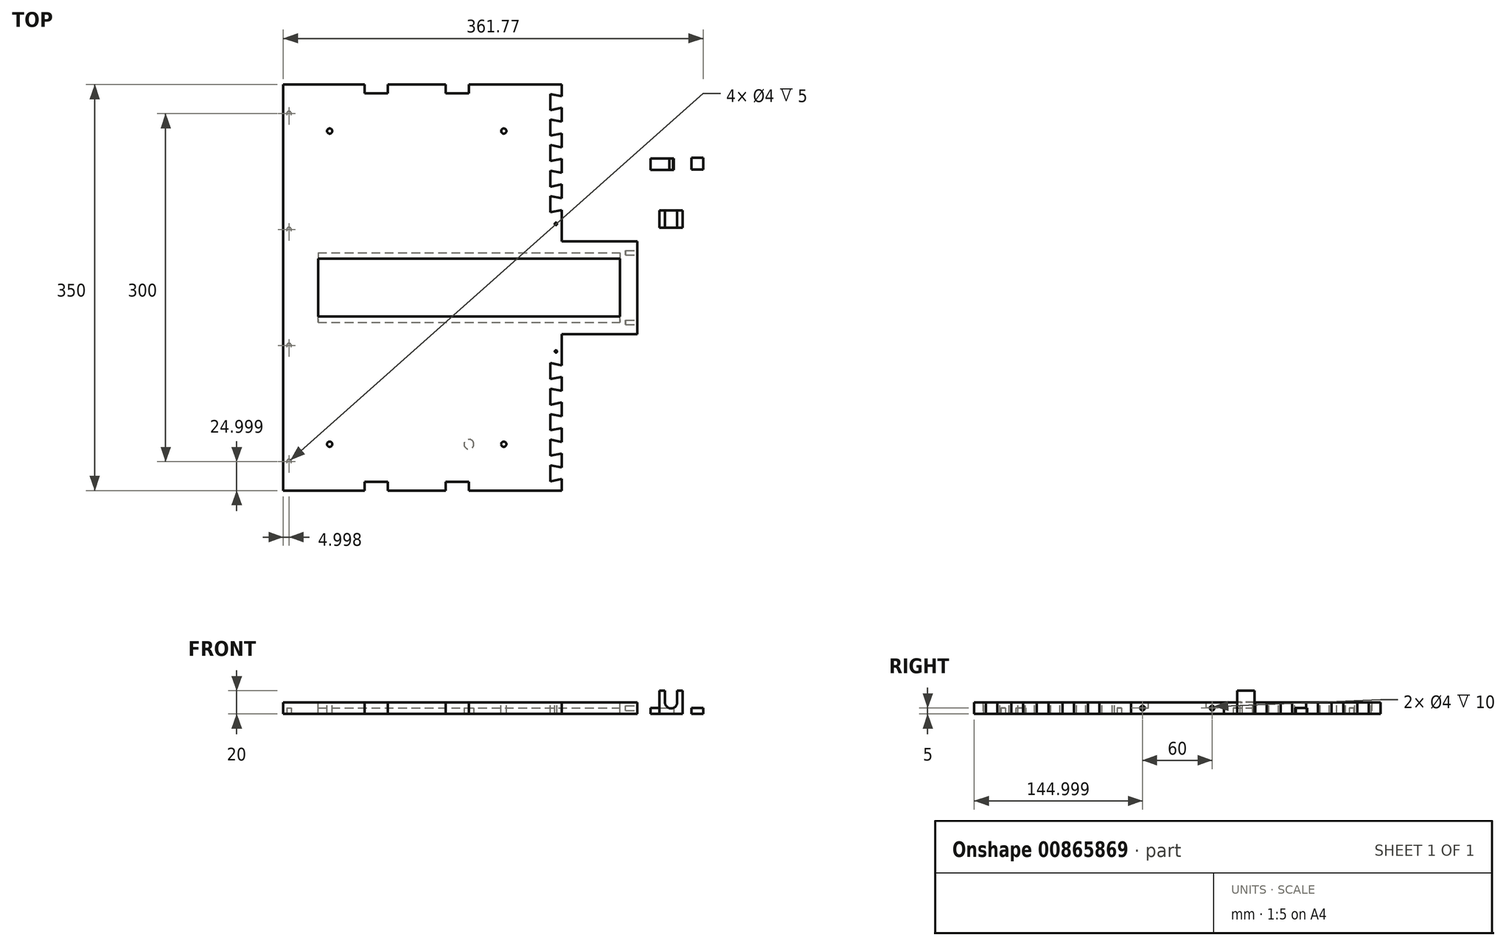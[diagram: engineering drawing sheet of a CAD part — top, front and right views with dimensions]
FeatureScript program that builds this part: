
annotation { "Feature Type Name" : "Feature", "Feature Type Description" : "" }
export const myFeature = defineFeature(function(context is Context, id is Id, definition is map)
    precondition{}
    {
        {
            var Q0;
            Q0=qCreatedBy(makeId("Top.planeOp"),FACE);
            var sketch = newSketch(context, id + "F0", { "sketchPlane" : qUnion([Q0])});
            skLineSegment(sketch, "E0.bottom", {"start": v(-223.21, 173.04) * mm, "end": v(-153.21, 173.04) * mm});
            skLineSegment(sketch, "E0.top", {"start": v(-223.21, -176.96) * mm, "end": v(-153.21, -176.96) * mm});
            skLineSegment(sketch, "E0.left", {"start": v(-223.21, 173.04) * mm, "end": v(-223.21, -176.96) * mm});
            skLineSegment(sketch, "E1.bottom", {"start": v(16.79, 38.04) * mm, "end": v(81.79, 38.04) * mm});
            skLineSegment(sketch, "E1.top", {"start": v(16.79, -41.96) * mm, "end": v(81.79, -41.96) * mm});
            skLineSegment(sketch, "E1.right", {"start": v(81.79, 38.04) * mm, "end": v(81.79, -41.96) * mm});
            skLineSegment(sketch, "E2", {"start": v(-153.21, -176.96) * mm, "end": v(-153.21, -169.46) * mm});
            skLineSegment(sketch, "E3", {"start": v(-153.21, -169.46) * mm, "end": v(-133.21, -169.46) * mm});
            skLineSegment(sketch, "E4", {"start": v(-133.21, -169.46) * mm, "end": v(-133.21, -176.96) * mm});
            skLineSegment(sketch, "E5", {"start": v(-83.21, -176.96) * mm, "end": v(-83.21, -169.46) * mm});
            skLineSegment(sketch, "E6", {"start": v(-83.21, -169.46) * mm, "end": v(-63.21, -169.46) * mm});
            skLineSegment(sketch, "E7", {"start": v(-63.21, -169.46) * mm, "end": v(-63.21, -176.96) * mm});
            skLineSegment(sketch, "E8", {"start": v(-153.21, 173.04) * mm, "end": v(-153.21, 165.54) * mm});
            skLineSegment(sketch, "E9", {"start": v(-153.21, 165.54) * mm, "end": v(-133.21, 165.54) * mm});
            skLineSegment(sketch, "E10", {"start": v(-133.21, 165.54) * mm, "end": v(-133.21, 173.04) * mm});
            skLineSegment(sketch, "E11", {"start": v(-83.21, 173.04) * mm, "end": v(-83.21, 165.54) * mm});
            skLineSegment(sketch, "E12", {"start": v(-83.21, 165.54) * mm, "end": v(-63.21, 165.54) * mm});
            skLineSegment(sketch, "E13", {"start": v(-63.21, 165.54) * mm, "end": v(-63.21, 173.04) * mm});
            skLineSegment(sketch, "E14.trimOffspring", {"start": v(-133.21, 173.04) * mm, "end": v(-83.21, 173.04) * mm});
            skLineSegment(sketch, "E15.trimOffspring", {"start": v(-63.21, 173.04) * mm, "end": v(16.79, 173.04) * mm});
            skLineSegment(sketch, "E16.trimOffspring", {"start": v(-133.21, -176.96) * mm, "end": v(-83.21, -176.96) * mm});
            skLineSegment(sketch, "E17.trimOffspring", {"start": v(-63.21, -176.96) * mm, "end": v(16.79, -176.96) * mm});
            skLineSegment(sketch, "E18", {"start": v(16.79, -41.96) * mm, "end": v(16.79, -176.96) * mm});
            skLineSegment(sketch, "E19", {"start": v(16.79, 173.04) * mm, "end": v(16.79, 38.04) * mm});
            skSolve(sketch);
        }
        {
            var Q0;
            Q0 = qSketchRegion(id + "F0", true);
            extrude(context, id + "F1", {"entities" : qUnion([Q0]), "depth" : 10 * mm, "offsetDistance" : 25 * mm});
        }
        {
            var Q0;
            Q0=makeQuery(id+"F1.opExtrude","CAP_FACE",FACE,{"disambiguationData":[OSD([sQuery(id+"F0.wireOp",EDGE,"E0.bottom"),sQuery(id+"F0.wireOp",EDGE,"E0.top"),sQuery(id+"F0.wireOp",EDGE,"E0.left"),sQuery(id+"F0.wireOp",EDGE,"E0.right"),sQuery(id+"F0.wireOp",EDGE,"E1.bottom"),sQuery(id+"F0.wireOp",EDGE,"E1.top"),sQuery(id+"F0.wireOp",EDGE,"E1.right"),sQuery(id+"F0.wireOp",EDGE,"E2"),sQuery(id+"F0.wireOp",EDGE,"E3"),sQuery(id+"F0.wireOp",EDGE,"E4"),sQuery(id+"F0.wireOp",EDGE,"E5"),sQuery(id+"F0.wireOp",EDGE,"E6"),sQuery(id+"F0.wireOp",EDGE,"E7"),sQuery(id+"F0.wireOp",EDGE,"E8"),sQuery(id+"F0.wireOp",EDGE,"E9"),sQuery(id+"F0.wireOp",EDGE,"E10"),sQuery(id+"F0.wireOp",EDGE,"E11"),sQuery(id+"F0.wireOp",EDGE,"E12"),sQuery(id+"F0.wireOp",EDGE,"E13"),sQuery(id+"F0.wireOp",EDGE,"E14.trimOffspring"),sQuery(id+"F0.wireOp",EDGE,"E15.trimOffspring"),sQuery(id+"F0.wireOp",EDGE,"E16.trimOffspring"),sQuery(id+"F0.wireOp",EDGE,"E17.trimOffspring"),sQuery(id+"F0.wireOp",EDGE,"d612cc93-a2dd-4ca0-8a1d-24db4bd78f01.trimOffspring"),sQuery(id+"F0.wireOp",EDGE,"VUu9vlwh-scEU-5erY-qjFF-pzVOPnd5OPAv"),sQuery(id+"F0.wireOp",EDGE,"Mesl0YVq-1EAC-d2jV-bsOK-wMALHSYDG3NM"),sQuery(id+"F0.wireOp",EDGE,"92T8g2C6-nla1-RGQU-U8xP-0400sJSxDG5c"),sQuery(id+"F0.wireOp",EDGE,"8OttDziy-c3AC-nBwE-2vRi-LbN1xkyNv4S0"),sQuery(id+"F0.wireOp",EDGE,"olr9cFaj-wmcz-6iY7-7Rzk-0wIROpixpfNE"),sQuery(id+"F0.wireOp",EDGE,"gA334X8u-PkTN-EDb3-7s9l-FT2O3QUcBCii"),sQuery(id+"F0.wireOp",EDGE,"2W5brfAA-w2qS-zJ9u-xPJi-NcULJrRPswGo"),sQuery(id+"F0.wireOp",EDGE,"luCa4cxE-H1tV-c6ab-pDNL-xg3xlzjdEsyn"),sQuery(id+"F0.wireOp",EDGE,"lG8ZVKkz-6INt-8FFC-6SXb-zNrBTEiRuwl3"),sQuery(id+"F0.wireOp",EDGE,"XRRxn0Ou-MKkb-N5V8-Fc5L-teCLoHKRe5wq"),sQuery(id+"F0.wireOp",EDGE,"wRixlGXv-lyk0-Hawx-yPcE-yobWA8MM16vS"),sQuery(id+"F0.wireOp",EDGE,"6DYoSN1p-wePG-CHtV-O8LX-gUoD5BVTUscE"),sQuery(id+"F0.wireOp",EDGE,"7xG2Ml0I-4bGv-ebdC-AR4S-G1sii3d71s1m"),sQuery(id+"F0.wireOp",EDGE,"Riv4Mbvf-Fbdf-Y5cd-fsFX-eB2JetC9W9YG"),sQuery(id+"F0.wireOp",EDGE,"No0oerPV-7ng4-ggHj-k2Vg-0BrW91tESk6H"),sQuery(id+"F0.wireOp",EDGE,"f2yUet7i-MCtZ-KdoX-q0Co-NCC2tnTZev2N"),sQuery(id+"F0.wireOp",EDGE,"cGX4Fyby-ReKv-VlGi-A0E8-5zCFY62Pwgkj"),sQuery(id+"F0.wireOp",EDGE,"Zo89N1cU-t1EY-i8rY-Yv0w-8HGAqcnqHVZ5"),sQuery(id+"F0.wireOp",EDGE,"DMeGy8ph-MtYO-7ydG-EfxJ-TsB1V2bi2QTX"),sQuery(id+"F0.wireOp",EDGE,"GU6erTmp-wWMu-GeIu-ZSqB-Ai4d9ksYpxLh"),sQuery(id+"F0.wireOp",EDGE,"VM02Z3jJ-Hq8z-eBe8-sUQo-V7Uc3UMlgatB"),sQuery(id+"F0.wireOp",EDGE,"HURvnJH2-qlYI-pxAH-gUDH-gB6cQl5a4oZ4"),sQuery(id+"F0.wireOp",EDGE,"j8azDgw8-tPOo-FNDL-AhCk-soEBbR0rcBn4"),sQuery(id+"F0.wireOp",EDGE,"5psSYCO1-JeF3-aQDp-G9BB-2fFlMMYLA1fD"),sQuery(id+"F0.wireOp",EDGE,"IoQ0W0ms-Jjoi-cpAW-Uph4-J6DpztlwMrAh"),sQuery(id+"F0.wireOp",EDGE,"C4cc451e-BhQn-YbQh-Ks1B-e5sdskLCcCkq"),sQuery(id+"F0.wireOp",EDGE,"JP3llaVh-4ocy-Qo8B-h7ym-UVwgTFmV5AdQ"),sQuery(id+"F0.wireOp",EDGE,"oXysVJYb-0DBb-emN8-Xvst-VYyeLteeISUo"),sQuery(id+"F0.wireOp",EDGE,"Cju6UDPM-zIzj-Fp70-kH6f-vF9RBWN7DGAg"),sQuery(id+"F0.wireOp",EDGE,"22R725SO-wWLv-bTEq-q8Rq-E17I1sVz65Jl"),sQuery(id+"F0.wireOp",EDGE,"pQkVYeNs-2zxO-owCs-zshn-SGN6Id91Uhl0"),sQuery(id+"F0.wireOp",EDGE,"e8269c16-cdf6-423a-8d57-91271ef56259.trimOffspring"),sQuery(id+"F0.wireOp",EDGE,"76f2989b-e8d1-434e-9f96-fcbceb3fefd6.trimOffspring"),sQuery(id+"F0.wireOp",EDGE,"a18456e3-36a5-44f1-99bb-5f40aa3fc9c5.trimOffspring"),sQuery(id+"F0.wireOp",EDGE,"52bf8884-8e54-4fed-87ab-f0b074556f85.trimOffspring"),sQuery(id+"F0.wireOp",EDGE,"eb5965da-2bcc-4715-a714-38f941cf3d95.trimOffspring"),sQuery(id+"F0.wireOp",EDGE,"bffdb7a4-7fce-4798-b96e-8e5b3fee8715.trimOffspring"),sQuery(id+"F0.wireOp",EDGE,"92117c92-3e40-4a6a-b9ef-4308b91b1c67.trimOffspring"),sQuery(id+"F0.wireOp",EDGE,"ed20c765-09a2-4f30-b69b-66dea8f34fde.trimOffspring"),sQuery(id+"F0.wireOp",EDGE,"e6d0a249-cf73-4d61-a6b9-9cd2e6a2e819.trimOffspring")])],"isStart":false});
            var sketch = newSketch(context, id + "F2", { "sketchPlane" : qUnion([Q0])});
            skLineSegment(sketch, "E20.bottom", {"start": v(-193.21, 23.04) * mm, "end": v(66.79, 23.04) * mm});
            skLineSegment(sketch, "E20.top", {"start": v(-193.21, -26.96) * mm, "end": v(66.79, -26.96) * mm});
            skLineSegment(sketch, "E20.left", {"start": v(-193.21, 23.04) * mm, "end": v(-193.21, -26.96) * mm});
            skLineSegment(sketch, "E20.right", {"start": v(66.79, 23.04) * mm, "end": v(66.79, -26.96) * mm});
            skSolve(sketch);
        }
        {
            var Q0;
            Q0 = qSketchRegion(id + "F2", true);
            extrude(context, id + "F3", {"entities" : qUnion([Q0]), "operationType" : NewBodyOperationType.REMOVE, "endBound" : BoundingType.THROUGH_ALL, "oppositeDirection" : true, "depth" : 25 * mm, "offsetDistance" : 25 * mm});
        }
        {
            var Q0;
            Q0=makeQuery(id+"F3.boolean.opBoolean","COPY",FACE,{"derivedFrom":makeQuery(id+"F3.opExtrude","SWEPT_FACE",FACE,{"disambiguationData":[OSD([sQuery(id+"F2.wireOp",EDGE,"E20.bottom")])]})});
            var sketch = newSketch(context, id + "F4", { "sketchPlane" : qUnion([Q0])});
            skLineSegment(sketch, "E21.bottom", {"start": v(-193.21, 5) * mm, "end": v(66.79, 5) * mm});
            skLineSegment(sketch, "E21.top", {"start": v(-193.21, 0) * mm, "end": v(66.79, 0) * mm});
            skLineSegment(sketch, "E21.left", {"start": v(-193.21, 5) * mm, "end": v(-193.21, 0) * mm});
            skLineSegment(sketch, "E21.right", {"start": v(66.79, 5) * mm, "end": v(66.79, 0) * mm});
            skSolve(sketch);
        }
        {
            var Q0;
            Q0 = qSketchRegion(id + "F4", true);
            extrude(context, id + "F5", {"entities" : qUnion([Q0]), "operationType" : NewBodyOperationType.REMOVE, "oppositeDirection" : true, "depth" : 5 * mm, "offsetDistance" : 25 * mm});
        }
        {
            var Q0;
            Q0=makeQuery(id+"F3.boolean.opBoolean","COPY",FACE,{"derivedFrom":makeQuery(id+"F3.opExtrude","SWEPT_FACE",FACE,{"disambiguationData":[OSD([sQuery(id+"F2.wireOp",EDGE,"E20.top")])]})});
            var sketch = newSketch(context, id + "F6", { "sketchPlane" : qUnion([Q0])});
            skLineSegment(sketch, "E22.bottom", {"start": v(-66.79, 5) * mm, "end": v(193.21, 5) * mm});
            skLineSegment(sketch, "E22.top", {"start": v(-66.79, 0) * mm, "end": v(193.21, 0) * mm});
            skLineSegment(sketch, "E22.left", {"start": v(-66.79, 5) * mm, "end": v(-66.79, 0) * mm});
            skLineSegment(sketch, "E22.right", {"start": v(193.21, 5) * mm, "end": v(193.21, 0) * mm});
            skSolve(sketch);
        }
        {
            var Q0;
            Q0 = qSketchRegion(id + "F6", true);
            extrude(context, id + "F7", {"entities" : qUnion([Q0]), "operationType" : NewBodyOperationType.REMOVE, "oppositeDirection" : true, "depth" : 5 * mm, "offsetDistance" : 25 * mm});
        }
        {
            var Q0;
            Q0=makeQuery(id+"F1.opExtrude","CAP_FACE",FACE,{"disambiguationData":[OSD([sQuery(id+"F0.wireOp",EDGE,"E0.bottom"),sQuery(id+"F0.wireOp",EDGE,"E0.top"),sQuery(id+"F0.wireOp",EDGE,"E0.left"),sQuery(id+"F0.wireOp",EDGE,"E0.right"),sQuery(id+"F0.wireOp",EDGE,"E1.bottom"),sQuery(id+"F0.wireOp",EDGE,"E1.top"),sQuery(id+"F0.wireOp",EDGE,"E1.right"),sQuery(id+"F0.wireOp",EDGE,"E2"),sQuery(id+"F0.wireOp",EDGE,"E3"),sQuery(id+"F0.wireOp",EDGE,"E4"),sQuery(id+"F0.wireOp",EDGE,"E5"),sQuery(id+"F0.wireOp",EDGE,"E6"),sQuery(id+"F0.wireOp",EDGE,"E7"),sQuery(id+"F0.wireOp",EDGE,"E8"),sQuery(id+"F0.wireOp",EDGE,"E9"),sQuery(id+"F0.wireOp",EDGE,"E10"),sQuery(id+"F0.wireOp",EDGE,"E11"),sQuery(id+"F0.wireOp",EDGE,"E12"),sQuery(id+"F0.wireOp",EDGE,"E13"),sQuery(id+"F0.wireOp",EDGE,"E14.trimOffspring"),sQuery(id+"F0.wireOp",EDGE,"E15.trimOffspring"),sQuery(id+"F0.wireOp",EDGE,"E16.trimOffspring"),sQuery(id+"F0.wireOp",EDGE,"E17.trimOffspring"),sQuery(id+"F0.wireOp",EDGE,"d612cc93-a2dd-4ca0-8a1d-24db4bd78f01.trimOffspring"),sQuery(id+"F0.wireOp",EDGE,"VUu9vlwh-scEU-5erY-qjFF-pzVOPnd5OPAv"),sQuery(id+"F0.wireOp",EDGE,"Mesl0YVq-1EAC-d2jV-bsOK-wMALHSYDG3NM"),sQuery(id+"F0.wireOp",EDGE,"92T8g2C6-nla1-RGQU-U8xP-0400sJSxDG5c"),sQuery(id+"F0.wireOp",EDGE,"8OttDziy-c3AC-nBwE-2vRi-LbN1xkyNv4S0"),sQuery(id+"F0.wireOp",EDGE,"olr9cFaj-wmcz-6iY7-7Rzk-0wIROpixpfNE"),sQuery(id+"F0.wireOp",EDGE,"gA334X8u-PkTN-EDb3-7s9l-FT2O3QUcBCii"),sQuery(id+"F0.wireOp",EDGE,"2W5brfAA-w2qS-zJ9u-xPJi-NcULJrRPswGo"),sQuery(id+"F0.wireOp",EDGE,"luCa4cxE-H1tV-c6ab-pDNL-xg3xlzjdEsyn"),sQuery(id+"F0.wireOp",EDGE,"lG8ZVKkz-6INt-8FFC-6SXb-zNrBTEiRuwl3"),sQuery(id+"F0.wireOp",EDGE,"XRRxn0Ou-MKkb-N5V8-Fc5L-teCLoHKRe5wq"),sQuery(id+"F0.wireOp",EDGE,"wRixlGXv-lyk0-Hawx-yPcE-yobWA8MM16vS"),sQuery(id+"F0.wireOp",EDGE,"6DYoSN1p-wePG-CHtV-O8LX-gUoD5BVTUscE"),sQuery(id+"F0.wireOp",EDGE,"7xG2Ml0I-4bGv-ebdC-AR4S-G1sii3d71s1m"),sQuery(id+"F0.wireOp",EDGE,"Riv4Mbvf-Fbdf-Y5cd-fsFX-eB2JetC9W9YG"),sQuery(id+"F0.wireOp",EDGE,"No0oerPV-7ng4-ggHj-k2Vg-0BrW91tESk6H"),sQuery(id+"F0.wireOp",EDGE,"f2yUet7i-MCtZ-KdoX-q0Co-NCC2tnTZev2N"),sQuery(id+"F0.wireOp",EDGE,"cGX4Fyby-ReKv-VlGi-A0E8-5zCFY62Pwgkj"),sQuery(id+"F0.wireOp",EDGE,"Zo89N1cU-t1EY-i8rY-Yv0w-8HGAqcnqHVZ5"),sQuery(id+"F0.wireOp",EDGE,"DMeGy8ph-MtYO-7ydG-EfxJ-TsB1V2bi2QTX"),sQuery(id+"F0.wireOp",EDGE,"GU6erTmp-wWMu-GeIu-ZSqB-Ai4d9ksYpxLh"),sQuery(id+"F0.wireOp",EDGE,"VM02Z3jJ-Hq8z-eBe8-sUQo-V7Uc3UMlgatB"),sQuery(id+"F0.wireOp",EDGE,"HURvnJH2-qlYI-pxAH-gUDH-gB6cQl5a4oZ4"),sQuery(id+"F0.wireOp",EDGE,"j8azDgw8-tPOo-FNDL-AhCk-soEBbR0rcBn4"),sQuery(id+"F0.wireOp",EDGE,"5psSYCO1-JeF3-aQDp-G9BB-2fFlMMYLA1fD"),sQuery(id+"F0.wireOp",EDGE,"IoQ0W0ms-Jjoi-cpAW-Uph4-J6DpztlwMrAh"),sQuery(id+"F0.wireOp",EDGE,"C4cc451e-BhQn-YbQh-Ks1B-e5sdskLCcCkq"),sQuery(id+"F0.wireOp",EDGE,"JP3llaVh-4ocy-Qo8B-h7ym-UVwgTFmV5AdQ"),sQuery(id+"F0.wireOp",EDGE,"oXysVJYb-0DBb-emN8-Xvst-VYyeLteeISUo"),sQuery(id+"F0.wireOp",EDGE,"Cju6UDPM-zIzj-Fp70-kH6f-vF9RBWN7DGAg"),sQuery(id+"F0.wireOp",EDGE,"22R725SO-wWLv-bTEq-q8Rq-E17I1sVz65Jl"),sQuery(id+"F0.wireOp",EDGE,"pQkVYeNs-2zxO-owCs-zshn-SGN6Id91Uhl0"),sQuery(id+"F0.wireOp",EDGE,"e8269c16-cdf6-423a-8d57-91271ef56259.trimOffspring"),sQuery(id+"F0.wireOp",EDGE,"76f2989b-e8d1-434e-9f96-fcbceb3fefd6.trimOffspring"),sQuery(id+"F0.wireOp",EDGE,"a18456e3-36a5-44f1-99bb-5f40aa3fc9c5.trimOffspring"),sQuery(id+"F0.wireOp",EDGE,"52bf8884-8e54-4fed-87ab-f0b074556f85.trimOffspring"),sQuery(id+"F0.wireOp",EDGE,"eb5965da-2bcc-4715-a714-38f941cf3d95.trimOffspring"),sQuery(id+"F0.wireOp",EDGE,"bffdb7a4-7fce-4798-b96e-8e5b3fee8715.trimOffspring"),sQuery(id+"F0.wireOp",EDGE,"92117c92-3e40-4a6a-b9ef-4308b91b1c67.trimOffspring"),sQuery(id+"F0.wireOp",EDGE,"ed20c765-09a2-4f30-b69b-66dea8f34fde.trimOffspring"),sQuery(id+"F0.wireOp",EDGE,"e6d0a249-cf73-4d61-a6b9-9cd2e6a2e819.trimOffspring")])],"isStart":false});
            var sketch = newSketch(context, id + "F8", { "sketchPlane" : qUnion([Q0])});
            skCircle(sketch, "E23", {"center": v(-183.21, 133.04) * mm, "radius": 2.25 * mm});
            skCircle(sketch, "E24", {"center": v(-33.21, 133.04) * mm, "radius": 2.25 * mm});
            skCircle(sketch, "E25", {"center": v(-183.21, -136.96) * mm, "radius": 2.25 * mm});
            skCircle(sketch, "E26", {"center": v(-33.21, -136.96) * mm, "radius": 2.25 * mm});
            skSolve(sketch);
        }
        {
            var Q0;
            Q0 = qSketchRegion(id + "F8", true);
            extrude(context, id + "F9", {"entities" : qUnion([Q0]), "operationType" : NewBodyOperationType.REMOVE, "endBound" : BoundingType.THROUGH_ALL, "oppositeDirection" : true, "depth" : 25 * mm, "offsetDistance" : 25 * mm});
        }
        {
            var Q0;
            Q0=makeQuery(id+"F1.opExtrude","CAP_FACE",FACE,{"disambiguationData":[OSD([sQuery(id+"F0.wireOp",EDGE,"E0.bottom"),sQuery(id+"F0.wireOp",EDGE,"E0.top"),sQuery(id+"F0.wireOp",EDGE,"E0.left"),sQuery(id+"F0.wireOp",EDGE,"E0.right"),sQuery(id+"F0.wireOp",EDGE,"E1.bottom"),sQuery(id+"F0.wireOp",EDGE,"E1.top"),sQuery(id+"F0.wireOp",EDGE,"E1.right"),sQuery(id+"F0.wireOp",EDGE,"E2"),sQuery(id+"F0.wireOp",EDGE,"E3"),sQuery(id+"F0.wireOp",EDGE,"E4"),sQuery(id+"F0.wireOp",EDGE,"E5"),sQuery(id+"F0.wireOp",EDGE,"E6"),sQuery(id+"F0.wireOp",EDGE,"E7"),sQuery(id+"F0.wireOp",EDGE,"E8"),sQuery(id+"F0.wireOp",EDGE,"E9"),sQuery(id+"F0.wireOp",EDGE,"E10"),sQuery(id+"F0.wireOp",EDGE,"E11"),sQuery(id+"F0.wireOp",EDGE,"E12"),sQuery(id+"F0.wireOp",EDGE,"E13"),sQuery(id+"F0.wireOp",EDGE,"E14.trimOffspring"),sQuery(id+"F0.wireOp",EDGE,"E15.trimOffspring"),sQuery(id+"F0.wireOp",EDGE,"E16.trimOffspring"),sQuery(id+"F0.wireOp",EDGE,"E17.trimOffspring"),sQuery(id+"F0.wireOp",EDGE,"d612cc93-a2dd-4ca0-8a1d-24db4bd78f01.trimOffspring"),sQuery(id+"F0.wireOp",EDGE,"VUu9vlwh-scEU-5erY-qjFF-pzVOPnd5OPAv"),sQuery(id+"F0.wireOp",EDGE,"Mesl0YVq-1EAC-d2jV-bsOK-wMALHSYDG3NM"),sQuery(id+"F0.wireOp",EDGE,"92T8g2C6-nla1-RGQU-U8xP-0400sJSxDG5c"),sQuery(id+"F0.wireOp",EDGE,"8OttDziy-c3AC-nBwE-2vRi-LbN1xkyNv4S0"),sQuery(id+"F0.wireOp",EDGE,"olr9cFaj-wmcz-6iY7-7Rzk-0wIROpixpfNE"),sQuery(id+"F0.wireOp",EDGE,"gA334X8u-PkTN-EDb3-7s9l-FT2O3QUcBCii"),sQuery(id+"F0.wireOp",EDGE,"2W5brfAA-w2qS-zJ9u-xPJi-NcULJrRPswGo"),sQuery(id+"F0.wireOp",EDGE,"luCa4cxE-H1tV-c6ab-pDNL-xg3xlzjdEsyn"),sQuery(id+"F0.wireOp",EDGE,"lG8ZVKkz-6INt-8FFC-6SXb-zNrBTEiRuwl3"),sQuery(id+"F0.wireOp",EDGE,"XRRxn0Ou-MKkb-N5V8-Fc5L-teCLoHKRe5wq"),sQuery(id+"F0.wireOp",EDGE,"wRixlGXv-lyk0-Hawx-yPcE-yobWA8MM16vS"),sQuery(id+"F0.wireOp",EDGE,"6DYoSN1p-wePG-CHtV-O8LX-gUoD5BVTUscE"),sQuery(id+"F0.wireOp",EDGE,"7xG2Ml0I-4bGv-ebdC-AR4S-G1sii3d71s1m"),sQuery(id+"F0.wireOp",EDGE,"Riv4Mbvf-Fbdf-Y5cd-fsFX-eB2JetC9W9YG"),sQuery(id+"F0.wireOp",EDGE,"No0oerPV-7ng4-ggHj-k2Vg-0BrW91tESk6H"),sQuery(id+"F0.wireOp",EDGE,"f2yUet7i-MCtZ-KdoX-q0Co-NCC2tnTZev2N"),sQuery(id+"F0.wireOp",EDGE,"cGX4Fyby-ReKv-VlGi-A0E8-5zCFY62Pwgkj"),sQuery(id+"F0.wireOp",EDGE,"Zo89N1cU-t1EY-i8rY-Yv0w-8HGAqcnqHVZ5"),sQuery(id+"F0.wireOp",EDGE,"DMeGy8ph-MtYO-7ydG-EfxJ-TsB1V2bi2QTX"),sQuery(id+"F0.wireOp",EDGE,"GU6erTmp-wWMu-GeIu-ZSqB-Ai4d9ksYpxLh"),sQuery(id+"F0.wireOp",EDGE,"VM02Z3jJ-Hq8z-eBe8-sUQo-V7Uc3UMlgatB"),sQuery(id+"F0.wireOp",EDGE,"HURvnJH2-qlYI-pxAH-gUDH-gB6cQl5a4oZ4"),sQuery(id+"F0.wireOp",EDGE,"j8azDgw8-tPOo-FNDL-AhCk-soEBbR0rcBn4"),sQuery(id+"F0.wireOp",EDGE,"5psSYCO1-JeF3-aQDp-G9BB-2fFlMMYLA1fD"),sQuery(id+"F0.wireOp",EDGE,"IoQ0W0ms-Jjoi-cpAW-Uph4-J6DpztlwMrAh"),sQuery(id+"F0.wireOp",EDGE,"C4cc451e-BhQn-YbQh-Ks1B-e5sdskLCcCkq"),sQuery(id+"F0.wireOp",EDGE,"JP3llaVh-4ocy-Qo8B-h7ym-UVwgTFmV5AdQ"),sQuery(id+"F0.wireOp",EDGE,"oXysVJYb-0DBb-emN8-Xvst-VYyeLteeISUo"),sQuery(id+"F0.wireOp",EDGE,"Cju6UDPM-zIzj-Fp70-kH6f-vF9RBWN7DGAg"),sQuery(id+"F0.wireOp",EDGE,"22R725SO-wWLv-bTEq-q8Rq-E17I1sVz65Jl"),sQuery(id+"F0.wireOp",EDGE,"pQkVYeNs-2zxO-owCs-zshn-SGN6Id91Uhl0"),sQuery(id+"F0.wireOp",EDGE,"e8269c16-cdf6-423a-8d57-91271ef56259.trimOffspring"),sQuery(id+"F0.wireOp",EDGE,"76f2989b-e8d1-434e-9f96-fcbceb3fefd6.trimOffspring"),sQuery(id+"F0.wireOp",EDGE,"a18456e3-36a5-44f1-99bb-5f40aa3fc9c5.trimOffspring"),sQuery(id+"F0.wireOp",EDGE,"52bf8884-8e54-4fed-87ab-f0b074556f85.trimOffspring"),sQuery(id+"F0.wireOp",EDGE,"eb5965da-2bcc-4715-a714-38f941cf3d95.trimOffspring"),sQuery(id+"F0.wireOp",EDGE,"bffdb7a4-7fce-4798-b96e-8e5b3fee8715.trimOffspring"),sQuery(id+"F0.wireOp",EDGE,"92117c92-3e40-4a6a-b9ef-4308b91b1c67.trimOffspring"),sQuery(id+"F0.wireOp",EDGE,"ed20c765-09a2-4f30-b69b-66dea8f34fde.trimOffspring"),sQuery(id+"F0.wireOp",EDGE,"e6d0a249-cf73-4d61-a6b9-9cd2e6a2e819.trimOffspring")])],"isStart":true});
            var sketch = newSketch(context, id + "F10", { "sketchPlane" : qUnion([Q0])});
            skCircle(sketch, "E27", {"center": v(-63.21, 136.96) * mm, "radius": 4.25 * mm});
            skCircle(sketch, "E28", {"center": v(-218.21, 151.96) * mm, "radius": 2 * mm});
            skCircle(sketch, "E29", {"center": v(-218.21, 51.96) * mm, "radius": 2 * mm});
            skCircle(sketch, "E30", {"center": v(-218.21, -48.04) * mm, "radius": 2 * mm});
            skCircle(sketch, "E31", {"center": v(-218.21, -148.04) * mm, "radius": 2 * mm});
            skSolve(sketch);
        }
        {
            var Q0;
            Q0 = qSketchRegion(id + "F10", true);
            extrude(context, id + "F11", {"entities" : qUnion([Q0]), "operationType" : NewBodyOperationType.REMOVE, "oppositeDirection" : true, "depth" : 5 * mm, "offsetDistance" : 25 * mm});
        }
        {
            var Q0;
            Q0=makeQuery(id+"F1.opExtrude","CAP_FACE",FACE,{"disambiguationData":[OSD([sQuery(id+"F0.wireOp",EDGE,"E0.bottom"),sQuery(id+"F0.wireOp",EDGE,"E0.top"),sQuery(id+"F0.wireOp",EDGE,"E0.left"),sQuery(id+"F0.wireOp",EDGE,"E0.right"),sQuery(id+"F0.wireOp",EDGE,"E1.bottom"),sQuery(id+"F0.wireOp",EDGE,"E1.top"),sQuery(id+"F0.wireOp",EDGE,"E1.right"),sQuery(id+"F0.wireOp",EDGE,"E2"),sQuery(id+"F0.wireOp",EDGE,"E3"),sQuery(id+"F0.wireOp",EDGE,"E4"),sQuery(id+"F0.wireOp",EDGE,"E5"),sQuery(id+"F0.wireOp",EDGE,"E6"),sQuery(id+"F0.wireOp",EDGE,"E7"),sQuery(id+"F0.wireOp",EDGE,"E8"),sQuery(id+"F0.wireOp",EDGE,"E9"),sQuery(id+"F0.wireOp",EDGE,"E10"),sQuery(id+"F0.wireOp",EDGE,"E11"),sQuery(id+"F0.wireOp",EDGE,"E12"),sQuery(id+"F0.wireOp",EDGE,"E13"),sQuery(id+"F0.wireOp",EDGE,"E14.trimOffspring"),sQuery(id+"F0.wireOp",EDGE,"E15.trimOffspring"),sQuery(id+"F0.wireOp",EDGE,"E16.trimOffspring"),sQuery(id+"F0.wireOp",EDGE,"E17.trimOffspring"),sQuery(id+"F0.wireOp",EDGE,"d612cc93-a2dd-4ca0-8a1d-24db4bd78f01.trimOffspring"),sQuery(id+"F0.wireOp",EDGE,"VUu9vlwh-scEU-5erY-qjFF-pzVOPnd5OPAv"),sQuery(id+"F0.wireOp",EDGE,"Mesl0YVq-1EAC-d2jV-bsOK-wMALHSYDG3NM"),sQuery(id+"F0.wireOp",EDGE,"92T8g2C6-nla1-RGQU-U8xP-0400sJSxDG5c"),sQuery(id+"F0.wireOp",EDGE,"8OttDziy-c3AC-nBwE-2vRi-LbN1xkyNv4S0"),sQuery(id+"F0.wireOp",EDGE,"olr9cFaj-wmcz-6iY7-7Rzk-0wIROpixpfNE"),sQuery(id+"F0.wireOp",EDGE,"gA334X8u-PkTN-EDb3-7s9l-FT2O3QUcBCii"),sQuery(id+"F0.wireOp",EDGE,"2W5brfAA-w2qS-zJ9u-xPJi-NcULJrRPswGo"),sQuery(id+"F0.wireOp",EDGE,"luCa4cxE-H1tV-c6ab-pDNL-xg3xlzjdEsyn"),sQuery(id+"F0.wireOp",EDGE,"lG8ZVKkz-6INt-8FFC-6SXb-zNrBTEiRuwl3"),sQuery(id+"F0.wireOp",EDGE,"XRRxn0Ou-MKkb-N5V8-Fc5L-teCLoHKRe5wq"),sQuery(id+"F0.wireOp",EDGE,"wRixlGXv-lyk0-Hawx-yPcE-yobWA8MM16vS"),sQuery(id+"F0.wireOp",EDGE,"6DYoSN1p-wePG-CHtV-O8LX-gUoD5BVTUscE"),sQuery(id+"F0.wireOp",EDGE,"7xG2Ml0I-4bGv-ebdC-AR4S-G1sii3d71s1m"),sQuery(id+"F0.wireOp",EDGE,"Riv4Mbvf-Fbdf-Y5cd-fsFX-eB2JetC9W9YG"),sQuery(id+"F0.wireOp",EDGE,"No0oerPV-7ng4-ggHj-k2Vg-0BrW91tESk6H"),sQuery(id+"F0.wireOp",EDGE,"f2yUet7i-MCtZ-KdoX-q0Co-NCC2tnTZev2N"),sQuery(id+"F0.wireOp",EDGE,"cGX4Fyby-ReKv-VlGi-A0E8-5zCFY62Pwgkj"),sQuery(id+"F0.wireOp",EDGE,"Zo89N1cU-t1EY-i8rY-Yv0w-8HGAqcnqHVZ5"),sQuery(id+"F0.wireOp",EDGE,"DMeGy8ph-MtYO-7ydG-EfxJ-TsB1V2bi2QTX"),sQuery(id+"F0.wireOp",EDGE,"GU6erTmp-wWMu-GeIu-ZSqB-Ai4d9ksYpxLh"),sQuery(id+"F0.wireOp",EDGE,"VM02Z3jJ-Hq8z-eBe8-sUQo-V7Uc3UMlgatB"),sQuery(id+"F0.wireOp",EDGE,"HURvnJH2-qlYI-pxAH-gUDH-gB6cQl5a4oZ4"),sQuery(id+"F0.wireOp",EDGE,"j8azDgw8-tPOo-FNDL-AhCk-soEBbR0rcBn4"),sQuery(id+"F0.wireOp",EDGE,"5psSYCO1-JeF3-aQDp-G9BB-2fFlMMYLA1fD"),sQuery(id+"F0.wireOp",EDGE,"IoQ0W0ms-Jjoi-cpAW-Uph4-J6DpztlwMrAh"),sQuery(id+"F0.wireOp",EDGE,"C4cc451e-BhQn-YbQh-Ks1B-e5sdskLCcCkq"),sQuery(id+"F0.wireOp",EDGE,"JP3llaVh-4ocy-Qo8B-h7ym-UVwgTFmV5AdQ"),sQuery(id+"F0.wireOp",EDGE,"oXysVJYb-0DBb-emN8-Xvst-VYyeLteeISUo"),sQuery(id+"F0.wireOp",EDGE,"Cju6UDPM-zIzj-Fp70-kH6f-vF9RBWN7DGAg"),sQuery(id+"F0.wireOp",EDGE,"22R725SO-wWLv-bTEq-q8Rq-E17I1sVz65Jl"),sQuery(id+"F0.wireOp",EDGE,"pQkVYeNs-2zxO-owCs-zshn-SGN6Id91Uhl0"),sQuery(id+"F0.wireOp",EDGE,"e8269c16-cdf6-423a-8d57-91271ef56259.trimOffspring"),sQuery(id+"F0.wireOp",EDGE,"76f2989b-e8d1-434e-9f96-fcbceb3fefd6.trimOffspring"),sQuery(id+"F0.wireOp",EDGE,"a18456e3-36a5-44f1-99bb-5f40aa3fc9c5.trimOffspring"),sQuery(id+"F0.wireOp",EDGE,"52bf8884-8e54-4fed-87ab-f0b074556f85.trimOffspring"),sQuery(id+"F0.wireOp",EDGE,"eb5965da-2bcc-4715-a714-38f941cf3d95.trimOffspring"),sQuery(id+"F0.wireOp",EDGE,"bffdb7a4-7fce-4798-b96e-8e5b3fee8715.trimOffspring"),sQuery(id+"F0.wireOp",EDGE,"92117c92-3e40-4a6a-b9ef-4308b91b1c67.trimOffspring"),sQuery(id+"F0.wireOp",EDGE,"ed20c765-09a2-4f30-b69b-66dea8f34fde.trimOffspring"),sQuery(id+"F0.wireOp",EDGE,"e6d0a249-cf73-4d61-a6b9-9cd2e6a2e819.trimOffspring")])],"isStart":false});
            var sketch = newSketch(context, id + "F12", { "sketchPlane" : qUnion([Q0])});
            skCircle(sketch, "E32", {"center": v(11.79, -56.96) * mm, "radius": 1 * mm});
            skCircle(sketch, "E33", {"center": v(11.79, 53.04) * mm, "radius": 1 * mm});
            skSolve(sketch);
        }
        {
            var Q0;
            Q0 = qSketchRegion(id + "F12", true);
            extrude(context, id + "F13", {"entities" : qUnion([Q0]), "operationType" : NewBodyOperationType.REMOVE, "endBound" : BoundingType.THROUGH_ALL, "oppositeDirection" : true, "depth" : 5 * mm, "offsetDistance" : 25 * mm});
        }
        {
            var Q0;
            Q0=qCreatedBy(makeId("Top.planeOp"),FACE);
            var sketch = newSketch(context, id + "F14", { "sketchPlane" : qUnion([Q0])});
            skLineSegment(sketch, "E34.bottom", {"start": v(93.27, 109.4) * mm, "end": v(113.27, 109.4) * mm});
            skLineSegment(sketch, "E34.top", {"start": v(93.27, 99.4) * mm, "end": v(113.27, 99.4) * mm});
            skLineSegment(sketch, "E34.left", {"start": v(93.27, 109.4) * mm, "end": v(93.27, 99.4) * mm});
            skLineSegment(sketch, "E34.right", {"start": v(113.27, 109.4) * mm, "end": v(113.27, 99.4) * mm});
            skLineSegment(sketch, "E35.bottom", {"start": v(128.56, 110) * mm, "end": v(138.56, 110) * mm});
            skLineSegment(sketch, "E35.top", {"start": v(128.56, 100) * mm, "end": v(138.56, 100) * mm});
            skLineSegment(sketch, "E35.left", {"start": v(128.56, 110) * mm, "end": v(128.56, 100) * mm});
            skLineSegment(sketch, "E35.right", {"start": v(138.56, 110) * mm, "end": v(138.56, 100) * mm});
            skSolve(sketch);
        }
        {
            var Q0;
            Q0 = qSketchRegion(id + "F14", true);
            extrude(context, id + "F15", {"entities" : qUnion([Q0]), "depth" : 5 * mm, "offsetDistance" : 25 * mm});
        }
        {
            var Q0;
            Q0=qCreatedBy(makeId("Top.planeOp"),FACE);
            var sketch = newSketch(context, id + "F16", { "sketchPlane" : qUnion([Q0])});
            skLineSegment(sketch, "E36.bottom", {"start": v(100.97, 64.6) * mm, "end": v(120.97, 64.6) * mm});
            skLineSegment(sketch, "E36.top", {"start": v(100.97, 49.6) * mm, "end": v(120.97, 49.6) * mm});
            skLineSegment(sketch, "E36.left", {"start": v(100.97, 64.6) * mm, "end": v(100.97, 49.6) * mm});
            skLineSegment(sketch, "E36.right", {"start": v(120.97, 64.6) * mm, "end": v(120.97, 49.6) * mm});
            skSolve(sketch);
        }
        {
            var Q0;
            Q0 = qSketchRegion(id + "F16", true);
            extrude(context, id + "F17", {"entities" : qUnion([Q0]), "depth" : 20 * mm, "offsetDistance" : 25 * mm});
        }
        {
            var Q0;
            Q0=makeQuery(id+"F17.opExtrude","SWEPT_FACE",FACE,{"disambiguationData":[OSD([sQuery(id+"F16.wireOp",EDGE,"E36.top")])]});
            var sketch = newSketch(context, id + "F18", { "sketchPlane" : qUnion([Q0])});
            skArc(sketch, "E37", {"start": v(105.72, 10.07) * mm, "mid": v(110.94, 4.75) * mm, "end": v(116.22, 10) * mm});
            skLineSegment(sketch, "E38", {"start": v(105.72, 10.07) * mm, "end": v(105.72, 20) * mm});
            skLineSegment(sketch, "E39", {"start": v(116.22, 10) * mm, "end": v(116.22, 20) * mm});
            skLineSegment(sketch, "E40", {"start": v(116.22, 20) * mm, "end": v(105.72, 20) * mm});
            skSolve(sketch);
        }
        {
            var Q0;
            Q0 = qSketchRegion(id + "F18", true);
            extrude(context, id + "F19", {"entities" : qUnion([Q0]), "operationType" : NewBodyOperationType.REMOVE, "endBound" : BoundingType.THROUGH_ALL, "oppositeDirection" : true, "depth" : 25 * mm, "offsetDistance" : 25 * mm});
        }
        {
            var Q0;
            Q0=makeQuery(id+"F1.opExtrude","SWEPT_FACE",FACE,{"disambiguationData":[OSD([sQuery(id+"F0.wireOp",EDGE,"E1.right")])]});
            var sketch = newSketch(context, id + "F20", { "sketchPlane" : qUnion([Q0])});
            skCircle(sketch, "E41", {"center": v(-31.96, 5) * mm, "radius": 2 * mm});
            skPoint(sketch, "E41.centerSnap0", {"position": v(-41.96, 5) * mm});
            skCircle(sketch, "E42", {"center": v(28.04, 5) * mm, "radius": 2 * mm});
            skPoint(sketch, "E42.centerSnap0", {"position": v(38.04, 5) * mm});
            skSolve(sketch);
        }
        {
            var Q0;
            Q0 = qSketchRegion(id + "F20", true);
            extrude(context, id + "F21", {"entities" : qUnion([Q0]), "operationType" : NewBodyOperationType.REMOVE, "oppositeDirection" : true, "depth" : 10 * mm, "offsetDistance" : 25 * mm});
        }
        {
            var Q0;
            Q0=makeQuery(id+"F1.opExtrude","CAP_FACE",FACE,{"disambiguationData":[OSD([sQuery(id+"F0.wireOp",EDGE,"E0.bottom"),sQuery(id+"F0.wireOp",EDGE,"E0.top"),sQuery(id+"F0.wireOp",EDGE,"E0.left"),sQuery(id+"F0.wireOp",EDGE,"E1.bottom"),sQuery(id+"F0.wireOp",EDGE,"E1.top"),sQuery(id+"F0.wireOp",EDGE,"E1.right"),sQuery(id+"F0.wireOp",EDGE,"E2"),sQuery(id+"F0.wireOp",EDGE,"E3"),sQuery(id+"F0.wireOp",EDGE,"E4"),sQuery(id+"F0.wireOp",EDGE,"E5"),sQuery(id+"F0.wireOp",EDGE,"E6"),sQuery(id+"F0.wireOp",EDGE,"E7"),sQuery(id+"F0.wireOp",EDGE,"E8"),sQuery(id+"F0.wireOp",EDGE,"E9"),sQuery(id+"F0.wireOp",EDGE,"E10"),sQuery(id+"F0.wireOp",EDGE,"E11"),sQuery(id+"F0.wireOp",EDGE,"E12"),sQuery(id+"F0.wireOp",EDGE,"E13"),sQuery(id+"F0.wireOp",EDGE,"E14.trimOffspring"),sQuery(id+"F0.wireOp",EDGE,"E15.trimOffspring"),sQuery(id+"F0.wireOp",EDGE,"E16.trimOffspring"),sQuery(id+"F0.wireOp",EDGE,"E17.trimOffspring"),sQuery(id+"F0.wireOp",EDGE,"E18"),sQuery(id+"F0.wireOp",EDGE,"E19")])],"isStart":false});
            var sketch = newSketch(context, id + "F22", { "sketchPlane" : qUnion([Q0])});
            skLineSegment(sketch, "E43.0.1.0", {"start": v(16.79, -166.96) * mm, "end": v(6.79, -168.96) * mm});
            skLineSegment(sketch, "E43.0.1.1", {"start": v(6.79, -154.96) * mm, "end": v(16.79, -156.96) * mm});
            skLineSegment(sketch, "E43.0.1.2", {"start": v(16.79, -156.96) * mm, "end": v(16.79, -166.96) * mm});
            skLineSegment(sketch, "E43.0.1.3", {"start": v(6.79, -168.96) * mm, "end": v(6.79, -154.96) * mm});
            skLineSegment(sketch, "E44", {"start": v(16.79, 163.04) * mm, "end": v(6.79, 165.04) * mm});
            skLineSegment(sketch, "E45", {"start": v(6.79, 165.04) * mm, "end": v(6.79, 151.04) * mm});
            skLineSegment(sketch, "E46", {"start": v(6.79, 151.04) * mm, "end": v(16.79, 153.04) * mm});
            skLineSegment(sketch, "E47", {"start": v(16.79, 153.04) * mm, "end": v(16.79, 163.04) * mm});
            skLineSegment(sketch, "E48.0.1.0", {"start": v(6.79, 129.04) * mm, "end": v(16.79, 131.04) * mm});
            skLineSegment(sketch, "E48.0.1.1", {"start": v(16.79, 141.04) * mm, "end": v(6.79, 143.04) * mm});
            skLineSegment(sketch, "E48.0.1.2", {"start": v(6.79, 143.04) * mm, "end": v(6.79, 129.04) * mm});
            skLineSegment(sketch, "E48.0.1.3", {"start": v(16.79, 131.04) * mm, "end": v(16.79, 141.04) * mm});
            skLineSegment(sketch, "E48.0.2.0", {"start": v(6.79, 107.04) * mm, "end": v(16.79, 109.04) * mm});
            skLineSegment(sketch, "E48.0.2.1", {"start": v(16.79, 119.04) * mm, "end": v(6.79, 121.04) * mm});
            skLineSegment(sketch, "E48.0.2.2", {"start": v(6.79, 121.04) * mm, "end": v(6.79, 107.04) * mm});
            skLineSegment(sketch, "E48.0.2.3", {"start": v(16.79, 109.04) * mm, "end": v(16.79, 119.04) * mm});
            skLineSegment(sketch, "E48.0.3.0", {"start": v(6.79, 85.04) * mm, "end": v(16.79, 87.04) * mm});
            skLineSegment(sketch, "E48.0.3.1", {"start": v(16.79, 97.04) * mm, "end": v(6.79, 99.04) * mm});
            skLineSegment(sketch, "E48.0.3.2", {"start": v(6.79, 99.04) * mm, "end": v(6.79, 85.04) * mm});
            skLineSegment(sketch, "E48.0.3.3", {"start": v(16.79, 87.04) * mm, "end": v(16.79, 97.04) * mm});
            skLineSegment(sketch, "E48.direction1", {"start": v(6.79, 151.04) * mm, "end": v(31.79, 151.04) * mm, "construction": true});
            skLineSegment(sketch, "E48.direction2", {"start": v(6.79, 151.04) * mm, "end": v(6.79, 129.04) * mm, "construction": true});
            skLineSegment(sketch, "E49.0.1.0", {"start": v(16.79, -144.96) * mm, "end": v(6.79, -146.96) * mm});
            skLineSegment(sketch, "E49.0.1.1", {"start": v(6.79, -146.96) * mm, "end": v(6.79, -132.96) * mm});
            skLineSegment(sketch, "E49.0.1.2", {"start": v(6.79, -132.96) * mm, "end": v(16.79, -134.96) * mm});
            skLineSegment(sketch, "E49.0.1.3", {"start": v(16.79, -134.96) * mm, "end": v(16.79, -144.96) * mm});
            skLineSegment(sketch, "E49.0.2.0", {"start": v(16.79, -122.96) * mm, "end": v(6.79, -124.96) * mm});
            skLineSegment(sketch, "E49.0.2.1", {"start": v(6.79, -124.96) * mm, "end": v(6.79, -110.96) * mm});
            skLineSegment(sketch, "E49.0.2.2", {"start": v(6.79, -110.96) * mm, "end": v(16.79, -112.96) * mm});
            skLineSegment(sketch, "E49.0.2.3", {"start": v(16.79, -112.96) * mm, "end": v(16.79, -122.96) * mm});
            skLineSegment(sketch, "E49.0.3.0", {"start": v(16.79, -100.96) * mm, "end": v(6.79, -102.96) * mm});
            skLineSegment(sketch, "E49.0.3.1", {"start": v(6.79, -102.96) * mm, "end": v(6.79, -88.96) * mm});
            skLineSegment(sketch, "E49.0.3.2", {"start": v(6.79, -88.96) * mm, "end": v(16.79, -90.96) * mm});
            skLineSegment(sketch, "E49.0.3.3", {"start": v(16.79, -90.96) * mm, "end": v(16.79, -100.96) * mm});
            skLineSegment(sketch, "E49.direction1", {"start": v(6.79, -168.96) * mm, "end": v(31.79, -168.96) * mm, "construction": true});
            skLineSegment(sketch, "E49.direction2", {"start": v(6.79, -168.96) * mm, "end": v(6.79, -146.96) * mm, "construction": true});
            skLineSegment(sketch, "E50.0.0.4", {"start": v(6.79, 63.04) * mm, "end": v(16.79, 65.04) * mm});
            skLineSegment(sketch, "E50.3.0.4", {"start": v(16.79, 75.04) * mm, "end": v(6.79, 77.04) * mm});
            skLineSegment(sketch, "E50.6.0.4", {"start": v(6.79, 77.04) * mm, "end": v(6.79, 63.04) * mm});
            skLineSegment(sketch, "E50.9.0.4", {"start": v(16.79, 65.04) * mm, "end": v(16.79, 75.04) * mm});
            skLineSegment(sketch, "E51.0.0.4", {"start": v(16.79, -78.96) * mm, "end": v(6.79, -80.96) * mm});
            skLineSegment(sketch, "E51.3.0.4", {"start": v(6.79, -80.96) * mm, "end": v(6.79, -66.96) * mm});
            skLineSegment(sketch, "E51.6.0.4", {"start": v(6.79, -66.96) * mm, "end": v(16.79, -68.96) * mm});
            skLineSegment(sketch, "E51.9.0.4", {"start": v(16.79, -68.96) * mm, "end": v(16.79, -78.96) * mm});
            skSolve(sketch);
        }
        {
            var Q0;
            Q0 = qSketchRegion(id + "F22", true);
            extrude(context, id + "F23", {"entities" : qUnion([Q0]), "operationType" : NewBodyOperationType.REMOVE, "endBound" : BoundingType.THROUGH_ALL, "oppositeDirection" : true, "depth" : 25 * mm, "offsetDistance" : 25 * mm});
        }
    });
